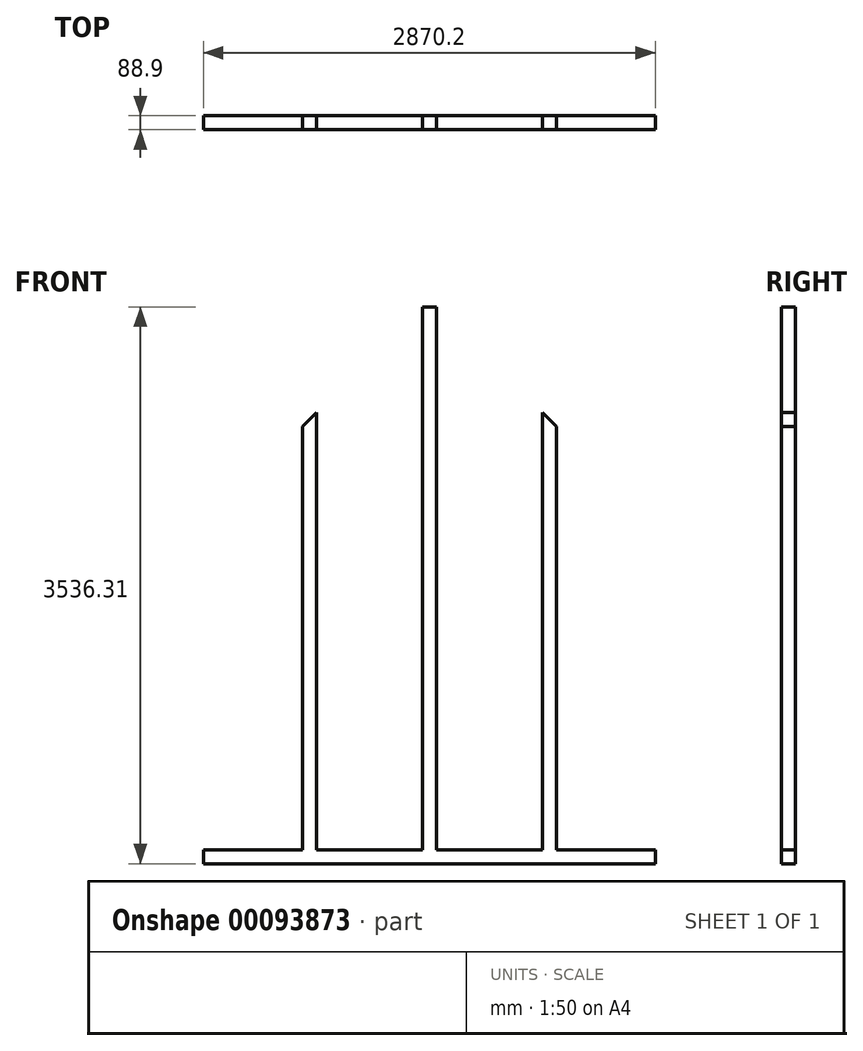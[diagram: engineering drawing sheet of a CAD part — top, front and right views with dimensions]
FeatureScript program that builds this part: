
annotation { "Feature Type Name" : "Feature", "Feature Type Description" : "" }
export const myFeature = defineFeature(function(context is Context, id is Id, definition is map)
    precondition{}
    {
        {
            var Q0;
            Q0=qCreatedBy(makeId("Front.planeOp"),FACE);
            var sketch = newSketch(context, id + "F0", { "sketchPlane" : qUnion([Q0])});
            skLineSegment(sketch, "E0.bottom", {"start": v(-1524, 0) * mm, "end": v(-1435.1, 0) * mm, "construction": true});
            skLineSegment(sketch, "E0.top", {"start": v(-1524, 2120.9) * mm, "end": v(-1435.1, 2120.9) * mm, "construction": true});
            skLineSegment(sketch, "E0.left", {"start": v(-1524, 0) * mm, "end": v(-1524, 2120.9) * mm, "construction": true});
            skLineSegment(sketch, "E0.right", {"start": v(1524, 0) * mm, "end": v(1524, 2120.9) * mm, "construction": true});
            skLineSegment(sketch, "E1", {"start": v(-1524, 2120.9) * mm, "end": v(0, 3644.9) * mm, "construction": true});
            skLineSegment(sketch, "E2", {"start": v(-1435.1, 2120.9) * mm, "end": v(-1435.1, 88.9) * mm, "construction": true});
            skLineSegment(sketch, "E3", {"start": v(-1435.1, 88.9) * mm, "end": v(-806.45, 88.9) * mm});
            skLineSegment(sketch, "E4", {"start": v(1435.1, 2120.9) * mm, "end": v(1435.1, 88.9) * mm, "construction": true});
            skLineSegment(sketch, "E5.trimOffspring", {"start": v(1435.1, 2120.9) * mm, "end": v(1524, 2120.9) * mm, "construction": true});
            skLineSegment(sketch, "E6", {"start": v(-1435.1, 88.9) * mm, "end": v(-1435.1, 0) * mm});
            skLineSegment(sketch, "E7", {"start": v(1435.1, 88.9) * mm, "end": v(1435.1, 0) * mm});
            skLineSegment(sketch, "E8", {"start": v(-1435.1, 0) * mm, "end": v(1435.1, 0) * mm});
            skLineSegment(sketch, "E9", {"start": v(1435.1, 0) * mm, "end": v(1524, 0) * mm, "construction": true});
            skLineSegment(sketch, "E10", {"start": v(0, 3644.9) * mm, "end": v(0, 0) * mm, "construction": true});
            skLineSegment(sketch, "E11", {"start": v(-762, 2882.9) * mm, "end": v(-762, 0) * mm, "construction": true});
            skLineSegment(sketch, "E12", {"start": v(762, 2870.84) * mm, "end": v(762, 0) * mm, "construction": true});
            skLineSegment(sketch, "E13", {"start": v(-806.45, 88.9) * mm, "end": v(-717.55, 88.9) * mm, "construction": true});
            skLineSegment(sketch, "E14", {"start": v(-717.55, 88.9) * mm, "end": v(-44.45, 88.9) * mm});
            skLineSegment(sketch, "E15", {"start": v(-44.45, 88.9) * mm, "end": v(44.45, 88.9) * mm, "construction": true});
            skLineSegment(sketch, "E16", {"start": v(44.45, 88.9) * mm, "end": v(717.55, 88.9) * mm});
            skLineSegment(sketch, "E17", {"start": v(717.55, 88.9) * mm, "end": v(806.45, 88.9) * mm, "construction": true});
            skLineSegment(sketch, "E18", {"start": v(806.45, 88.9) * mm, "end": v(1435.1, 88.9) * mm});
            skLineSegment(sketch, "E19", {"start": v(0, 3644.9) * mm, "end": v(1524, 2120.9) * mm, "construction": true});
            skLineSegment(sketch, "E20", {"start": v(-1467.17, 2114.87) * mm, "end": v(-705.17, 2876.87) * mm, "construction": true});
            skLineSegment(sketch, "E21", {"start": v(0, 3582.04) * mm, "end": v(1473.2, 2108.84) * mm, "construction": true});
            skLineSegment(sketch, "E22", {"start": v(-806.45, 2775.59) * mm, "end": v(-806.45, 88.9) * mm});
            skLineSegment(sketch, "E23", {"start": v(-705.17, 2876.87) * mm, "end": v(0, 3582.04) * mm, "construction": true});
            skLineSegment(sketch, "E24", {"start": v(-44.45, 3663.31) * mm, "end": v(-44.45, 3536.31) * mm, "construction": true});
            skLineSegment(sketch, "E25", {"start": v(44.45, 3663.31) * mm, "end": v(44.45, 3536.31) * mm, "construction": true});
            skLineSegment(sketch, "E26", {"start": v(717.55, 2864.49) * mm, "end": v(717.55, 88.9) * mm});
            skLineSegment(sketch, "E27", {"start": v(806.45, 2775.59) * mm, "end": v(806.45, 88.9) * mm});
            skLineSegment(sketch, "E28", {"start": v(-717.55, 2864.49) * mm, "end": v(-717.55, 88.9) * mm});
            skLineSegment(sketch, "E29", {"start": v(-806.45, 2775.59) * mm, "end": v(-705.17, 2876.87) * mm});
            skLineSegment(sketch, "E30", {"start": v(717.55, 2864.49) * mm, "end": v(806.45, 2775.59) * mm});
            skLineSegment(sketch, "E31", {"start": v(0, 3707.76) * mm, "end": v(-835.97, 2871.8) * mm, "construction": true});
            skLineSegment(sketch, "E32", {"start": v(-44.45, 3663.31) * mm, "end": v(44.45, 3663.31) * mm, "construction": true});
            skPoint(sketch, "E33.orphan", {"position": v(-44.45, 3600.45) * mm});
            skLineSegment(sketch, "E34", {"start": v(-44.45, 3536.31) * mm, "end": v(44.45, 3536.31) * mm});
            skLineSegment(sketch, "E35", {"start": v(-44.45, 3536.31) * mm, "end": v(-44.45, 88.9) * mm});
            skLineSegment(sketch, "E36", {"start": v(44.45, 3536.31) * mm, "end": v(44.45, 88.9) * mm});
            skSolve(sketch);
        }
        {
            var Q0;
            Q0=qSketchRegion(id+"F0",true);
            extrude(context, id + "F1", {"entities" : qUnion([Q0]), "depth" : 88.9 * mm});
        }
    });
